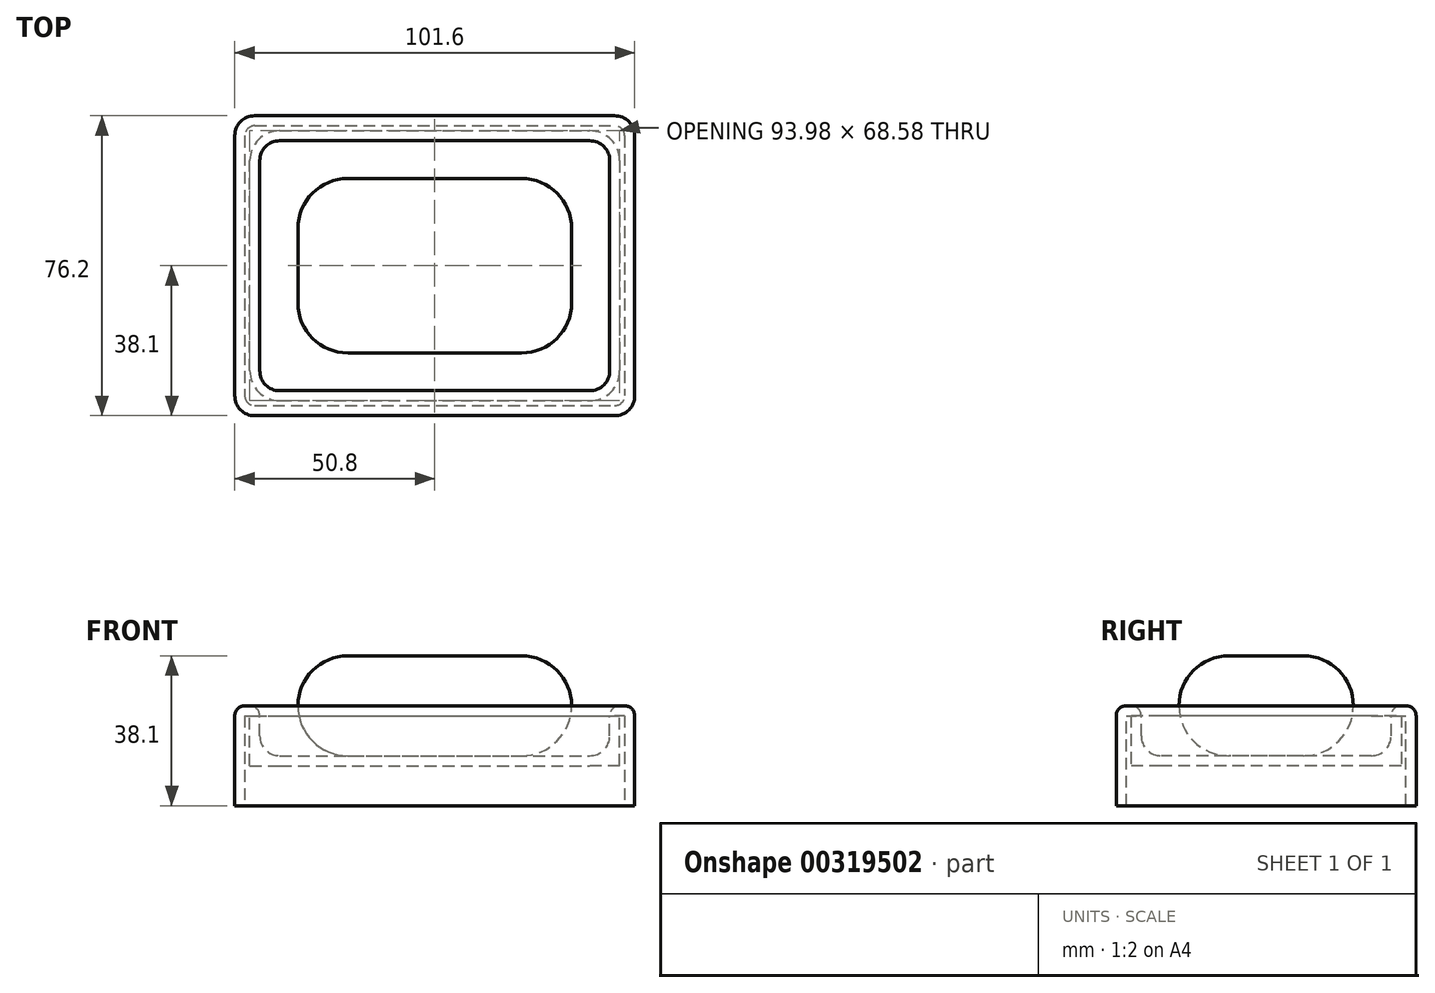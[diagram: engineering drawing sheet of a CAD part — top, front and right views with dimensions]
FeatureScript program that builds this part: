
annotation { "Feature Type Name" : "Feature", "Feature Type Description" : "" }
export const myFeature = defineFeature(function(context is Context, id is Id, definition is map)
    precondition{}
    {
        {
            var Q0;
            Q0=qCreatedBy(makeId("Top.planeOp"),FACE);
            var sketch = newSketch(context, id + "F0", { "sketchPlane" : qUnion([Q0])});
            skLineSegment(sketch, "E0.bottom", {"start": v(-50.8, 38.1) * mm, "end": v(50.8, 38.1) * mm});
            skLineSegment(sketch, "E0.top", {"start": v(-50.8, -38.1) * mm, "end": v(50.8, -38.1) * mm});
            skLineSegment(sketch, "E0.left", {"start": v(-50.8, 38.1) * mm, "end": v(-50.8, -38.1) * mm});
            skLineSegment(sketch, "E0.right", {"start": v(50.8, 38.1) * mm, "end": v(50.8, -38.1) * mm});
            skPoint(sketch, "E0.middle", {"position": v(0, 0) * mm});
            skSolve(sketch);
        }
        {
            var Q0;
            Q0=makeQuery(id+"F0.imprint","IMPRINT",FACE,{"disambiguationData":[TD([[makeQuery(id+"F0.imprint","IMPRINT",EDGE,{"derivedFrom":sQuery(id+"F0.wireOp",EDGE,"E0.bottom")}),-1.0]])]});
            extrude(context, id + "F1", {"entities" : qUnion([Q0]), "depth" : 25.4 * mm});
        }
        {
            var Q0;
            Q0=makeQuery(id+"F1.opExtrude","CAP_FACE",FACE,{"disambiguationData":[OSD([sQuery(id+"F0.wireOp",EDGE,"E0.bottom"),sQuery(id+"F0.wireOp",EDGE,"E0.top"),sQuery(id+"F0.wireOp",EDGE,"E0.left"),sQuery(id+"F0.wireOp",EDGE,"E0.right")])],"isStart":false});
            var sketch = newSketch(context, id + "F2", { "sketchPlane" : qUnion([Q0])});
            skLineSegment(sketch, "E1.bottom", {"start": v(-44.45, 31.75) * mm, "end": v(44.45, 31.75) * mm});
            skLineSegment(sketch, "E1.top", {"start": v(-44.45, -31.75) * mm, "end": v(44.45, -31.75) * mm});
            skLineSegment(sketch, "E1.left", {"start": v(-44.45, 31.75) * mm, "end": v(-44.45, -31.75) * mm});
            skLineSegment(sketch, "E1.right", {"start": v(44.45, 31.75) * mm, "end": v(44.45, -31.75) * mm});
            skPoint(sketch, "E1.middle", {"position": v(0, 0) * mm});
            skSolve(sketch);
        }
        {
            var Q0;
            Q0=makeQuery(id+"F2.imprint","IMPRINT",FACE,{"disambiguationData":[TD([[makeQuery(id+"F2.imprint","IMPRINT",EDGE,{"derivedFrom":sQuery(id+"F2.wireOp",EDGE,"E1.bottom")}),-1.0]])]});
            extrude(context, id + "F3", {"entities" : qUnion([Q0]), "operationType" : NewBodyOperationType.REMOVE, "oppositeDirection" : true, "depth" : 12.7 * mm});
        }
        {
            var Q0;
            Q0=makeQuery(id+"F3.boolean.opBoolean","COPY",EDGE,{"derivedFrom":makeQuery(id+"F3.opExtrude","SWEPT_EDGE",EDGE,{"disambiguationData":[OSD([sQuery(id+"F2.wireOp",EDGE,"E1.bottom"),sQuery(id+"F2.wireOp",EDGE,"E1.left")])]})});
            var Q1;
            Q1=makeQuery(id+"F3.boolean.opBoolean","COPY",EDGE,{"derivedFrom":makeQuery(id+"F3.opExtrude","SWEPT_EDGE",EDGE,{"disambiguationData":[OSD([sQuery(id+"F2.wireOp",EDGE,"E1.bottom"),sQuery(id+"F2.wireOp",EDGE,"E1.right")])]})});
            var Q2;
            Q2=makeQuery(id+"F3.boolean.opBoolean","COPY",EDGE,{"derivedFrom":makeQuery(id+"F3.opExtrude","SWEPT_EDGE",EDGE,{"disambiguationData":[OSD([sQuery(id+"F2.wireOp",EDGE,"E1.top"),sQuery(id+"F2.wireOp",EDGE,"E1.left")])]})});
            var Q3;
            Q3=makeQuery(id+"F3.boolean.opBoolean","COPY",EDGE,{"derivedFrom":makeQuery(id+"F3.opExtrude","SWEPT_EDGE",EDGE,{"disambiguationData":[OSD([sQuery(id+"F2.wireOp",EDGE,"E1.top"),sQuery(id+"F2.wireOp",EDGE,"E1.right")])]})});
            var Q4;
            Q4=makeQuery(id+"F1.opExtrude","SWEPT_EDGE",EDGE,{"disambiguationData":[OSD([sQuery(id+"F0.wireOp",EDGE,"E0.top"),sQuery(id+"F0.wireOp",EDGE,"E0.left")])]});
            var Q5;
            Q5=makeQuery(id+"F1.opExtrude","SWEPT_EDGE",EDGE,{"disambiguationData":[OSD([sQuery(id+"F0.wireOp",EDGE,"E0.top"),sQuery(id+"F0.wireOp",EDGE,"E0.right")])]});
            var Q6;
            Q6=makeQuery(id+"F1.opExtrude","SWEPT_EDGE",EDGE,{"disambiguationData":[OSD([sQuery(id+"F0.wireOp",EDGE,"E0.bottom"),sQuery(id+"F0.wireOp",EDGE,"E0.right")])]});
            var Q7;
            Q7=makeQuery(id+"F1.opExtrude","SWEPT_EDGE",EDGE,{"disambiguationData":[OSD([sQuery(id+"F0.wireOp",EDGE,"E0.bottom"),sQuery(id+"F0.wireOp",EDGE,"E0.left")])]});
            fillet(context, id + "F4", {"entities" : qUnion([Q0, Q1, Q2, Q3, Q4, Q5, Q6, Q7]), "radius" : 5.08 * mm, "tangentPropagation" : true, "allowEdgeOverflow" : false});
        }
        {
            var Q0;
            Q0=makeQuery(id+"F1.opExtrude","CAP_FACE",FACE,{"disambiguationData":[OSD([sQuery(id+"F0.wireOp",EDGE,"E0.bottom"),sQuery(id+"F0.wireOp",EDGE,"E0.top"),sQuery(id+"F0.wireOp",EDGE,"E0.left"),sQuery(id+"F0.wireOp",EDGE,"E0.right")])],"isStart":false});
            fillet(context, id + "F5", {"entities" : qUnion([Q0]), "radius" : 2.54 * mm, "tangentPropagation" : true, "allowEdgeOverflow" : false});
        }
        {
            var Q0;
            Q0=makeQuery(id+"F1.opExtrude","CAP_FACE",FACE,{"disambiguationData":[OSD([sQuery(id+"F0.wireOp",EDGE,"E0.bottom"),sQuery(id+"F0.wireOp",EDGE,"E0.top"),sQuery(id+"F0.wireOp",EDGE,"E0.left"),sQuery(id+"F0.wireOp",EDGE,"E0.right")])],"isStart":true});
            shell(context, id + "F6", {"entities" : qUnion([Q0]), "thickness" : 2.54 * mm});
        }
        {
            var Q0;
            Q0=makeQuery(id+"F3.boolean.opBoolean","COPY",FACE,{"derivedFrom":makeQuery(id+"F3.opExtrude","CAP_FACE",FACE,{"disambiguationData":[OSD([sQuery(id+"F2.wireOp",EDGE,"E1.bottom"),sQuery(id+"F2.wireOp",EDGE,"E1.top"),sQuery(id+"F2.wireOp",EDGE,"E1.left"),sQuery(id+"F2.wireOp",EDGE,"E1.right")])],"isStart":false})});
            var sketch = newSketch(context, id + "F7", { "sketchPlane" : qUnion([Q0])});
            skPoint(sketch, "E2.middle", {"position": v(0, 0) * mm});
            skLineSegment(sketch, "E3.bottom", {"start": v(-34.77, 22.16) * mm, "end": v(34.77, 22.16) * mm});
            skLineSegment(sketch, "E3.top", {"start": v(-34.77, -22.16) * mm, "end": v(34.77, -22.16) * mm});
            skLineSegment(sketch, "E3.left", {"start": v(-34.77, 22.16) * mm, "end": v(-34.77, -22.16) * mm});
            skLineSegment(sketch, "E3.right", {"start": v(34.77, 22.16) * mm, "end": v(34.77, -22.16) * mm});
            skSolve(sketch);
        }
        {
            var Q0;
            Q0 = qSketchRegion(id + "F7", true);
            extrude(context, id + "F8", {"entities" : qUnion([Q0]), "depth" : 25.4 * mm});
        }
        {
            var Q0;
            Q0=makeQuery(id+"F8.opExtrude","CAP_EDGE",EDGE,{"disambiguationData":[OSD([sQuery(id+"F7.wireOp",EDGE,"E3.right")])],"isStart":false});
            var Q1;
            Q1=makeQuery(id+"F8.opExtrude","SWEPT_EDGE",EDGE,{"disambiguationData":[OSD([sQuery(id+"F7.wireOp",EDGE,"E3.top"),sQuery(id+"F7.wireOp",EDGE,"E3.right")])]});
            var Q2;
            Q2=makeQuery(id+"F8.opExtrude","CAP_EDGE",EDGE,{"disambiguationData":[OSD([sQuery(id+"F7.wireOp",EDGE,"E3.right")])],"isStart":true});
            var Q3;
            Q3=makeQuery(id+"F8.opExtrude","SWEPT_EDGE",EDGE,{"disambiguationData":[OSD([sQuery(id+"F7.wireOp",EDGE,"E3.bottom"),sQuery(id+"F7.wireOp",EDGE,"E3.right")])]});
            var Q4;
            Q4=makeQuery(id+"F8.opExtrude","CAP_EDGE",EDGE,{"disambiguationData":[OSD([sQuery(id+"F7.wireOp",EDGE,"E3.bottom")])],"isStart":false});
            var Q5;
            Q5=makeQuery(id+"F8.opExtrude","CAP_EDGE",EDGE,{"disambiguationData":[OSD([sQuery(id+"F7.wireOp",EDGE,"E3.left")])],"isStart":false});
            var Q6;
            Q6=makeQuery(id+"F8.opExtrude","SWEPT_EDGE",EDGE,{"disambiguationData":[OSD([sQuery(id+"F7.wireOp",EDGE,"E3.top"),sQuery(id+"F7.wireOp",EDGE,"E3.left")])]});
            var Q7;
            Q7=makeQuery(id+"F8.opExtrude","CAP_EDGE",EDGE,{"disambiguationData":[OSD([sQuery(id+"F7.wireOp",EDGE,"E3.top")])],"isStart":false});
            var Q8;
            Q8=makeQuery(id+"F8.opExtrude","CAP_EDGE",EDGE,{"disambiguationData":[OSD([sQuery(id+"F7.wireOp",EDGE,"E3.top")])],"isStart":true});
            var Q9;
            Q9=makeQuery(id+"F8.opExtrude","CAP_EDGE",EDGE,{"disambiguationData":[OSD([sQuery(id+"F7.wireOp",EDGE,"E3.left")])],"isStart":true});
            var Q10;
            Q10=makeQuery(id+"F8.opExtrude","CAP_EDGE",EDGE,{"disambiguationData":[OSD([sQuery(id+"F7.wireOp",EDGE,"E3.bottom")])],"isStart":true});
            var Q11;
            Q11=makeQuery(id+"F8.opExtrude","SWEPT_EDGE",EDGE,{"disambiguationData":[OSD([sQuery(id+"F7.wireOp",EDGE,"E3.bottom"),sQuery(id+"F7.wireOp",EDGE,"E3.left")])]});
            fillet(context, id + "F9", {"entities" : qUnion([Q0, Q1, Q2, Q3, Q4, Q5, Q6, Q7, Q8, Q9, Q10, Q11]), "radius" : 12.7 * mm, "tangentPropagation" : true, "allowEdgeOverflow" : false});
        }
        {
            var Q0;
            Q0=makeQuery(id+"F3.boolean.opBoolean","COPY",EDGE,{"derivedFrom":makeQuery(id+"F3.opExtrude","CAP_EDGE",EDGE,{"disambiguationData":[OSD([sQuery(id+"F2.wireOp",EDGE,"E1.left")])],"isStart":false})});
            var Q1;
            Q1=makeQuery(id+"F3.boolean.opBoolean","COPY",EDGE,{"derivedFrom":makeQuery(id+"F3.opExtrude","CAP_EDGE",EDGE,{"disambiguationData":[OSD([sQuery(id+"F2.wireOp",EDGE,"E1.bottom")])],"isStart":false})});
            fillet(context, id + "F10", {"entities" : qUnion([Q0, Q1]), "radius" : 5.08 * mm, "tangentPropagation" : true, "allowEdgeOverflow" : false});
        }
    });
